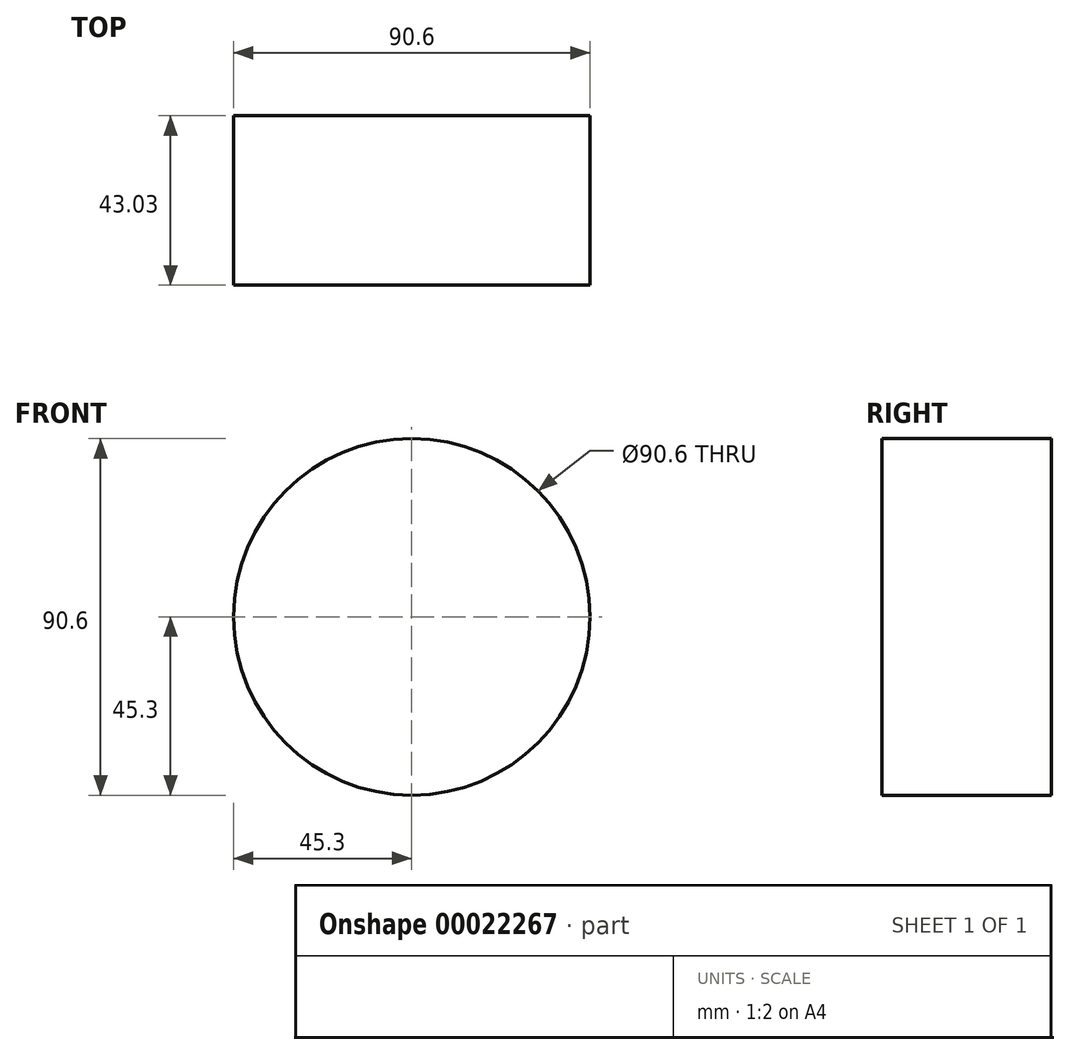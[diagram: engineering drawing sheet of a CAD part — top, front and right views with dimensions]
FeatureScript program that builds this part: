
annotation { "Feature Type Name" : "Feature", "Feature Type Description" : "" }
export const myFeature = defineFeature(function(context is Context, id is Id, definition is map)
    precondition{}
    {
        {
            var Q0;
            Q0=qCreatedBy(makeId("Front.planeOp"),FACE);
            var sketch = newSketch(context, id + "F0", { "sketchPlane" : qUnion([Q0])});
            skCircle(sketch, "E0", {"center": v(0, 0) * mm, "radius": 31.81 * mm});
            skSolve(sketch);
        }
        {
            var Q0;
            Q0=makeQuery(id+"F0.imprint","IMPRINT",FACE,{"disambiguationData":[TD([[makeQuery(id+"F0.imprint","IMPRINT",EDGE,{"derivedFrom":sQuery(id+"F0.wireOp",EDGE,"E0")}),1.0]])]});
            extrude(context, id + "F1", {"entities" : qUnion([Q0]), "depth" : 25.4 * mm});
        }
        {
            var Q0;
            Q0=qCreatedBy(makeId("Front.planeOp"),FACE);
            var sketch = newSketch(context, id + "F2", { "sketchPlane" : qUnion([Q0])});
            skCircle(sketch, "E1", {"center": v(0, 0) * mm, "radius": 45.3 * mm});
            skSolve(sketch);
        }
        {
            var Q0;
            Q0=sQuery(id+"F2.wireOp",EDGE,"E1");
            extrude(context, id + "F3", {"bodyType" : ToolBodyType.SURFACE, "surfaceEntities" : qUnion([Q0]), "oppositeDirection" : true, "depth" : 43.03 * mm});
        }
        {
            var Q0;
            Q0=makeQuery(id+"F1.opExtrude","SWEPT_BODY",BODY,{"disambiguationData":[OSD([sQuery(id+"F0.wireOp",EDGE,"E0")])]});
            deleteBodies(context, id + "F4", {"entities" : qUnion([Q0])});
        }
    });
